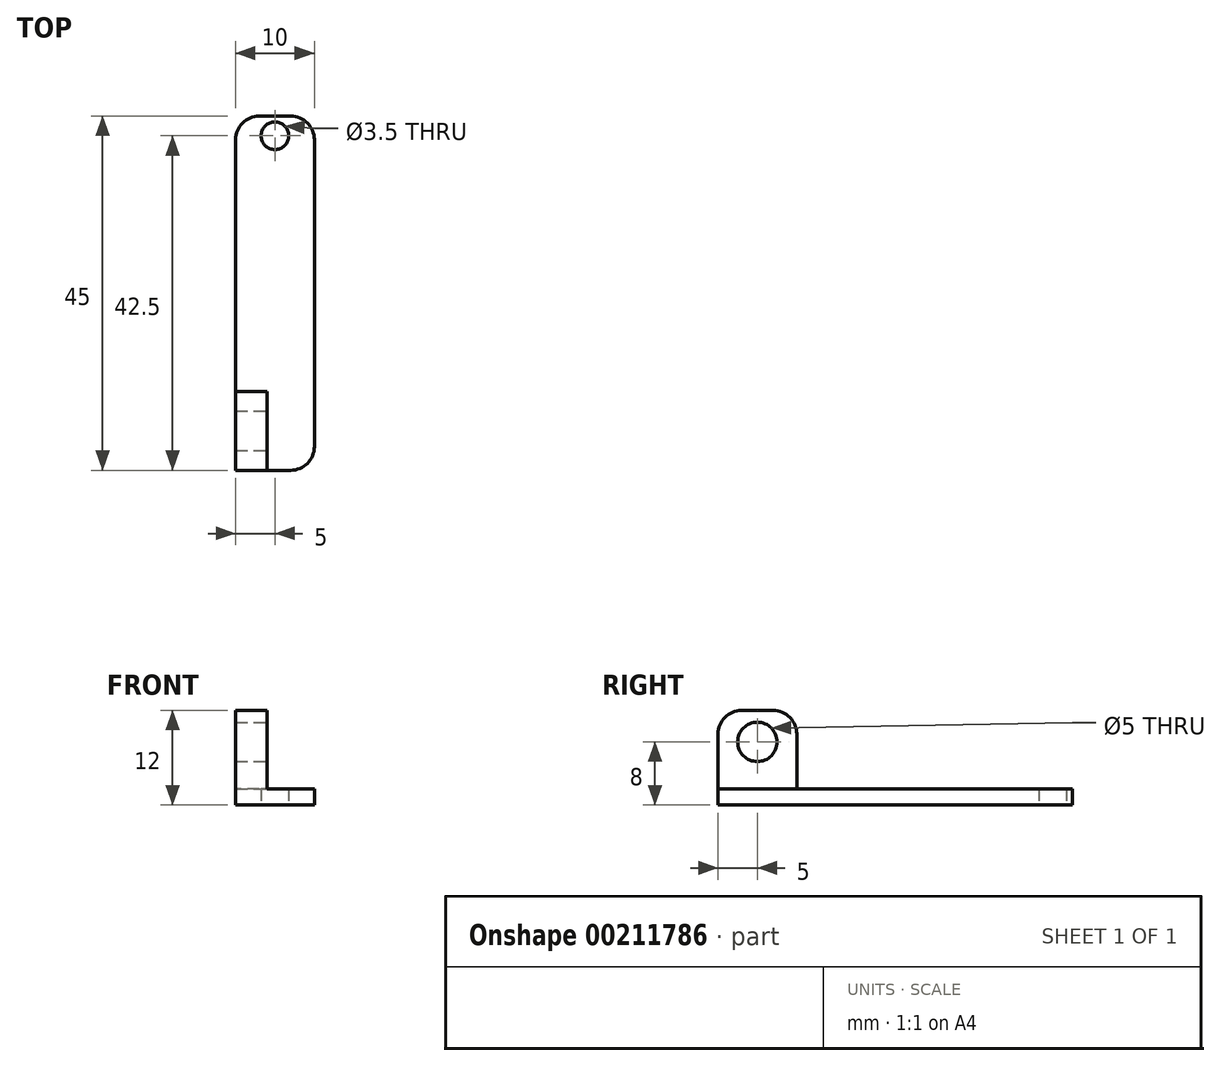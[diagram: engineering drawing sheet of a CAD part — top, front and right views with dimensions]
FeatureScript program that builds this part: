
annotation { "Feature Type Name" : "Feature", "Feature Type Description" : "" }
export const myFeature = defineFeature(function(context is Context, id is Id, definition is map)
    precondition{}
    {
        {
            var Q0;
            Q0=qCreatedBy(makeId("Top.planeOp"),FACE);
            var sketch = newSketch(context, id + "F0", { "sketchPlane" : qUnion([Q0])});
            skLineSegment(sketch, "E0.bottom", {"start": v(0, 0) * mm, "end": v(10, 0) * mm});
            skLineSegment(sketch, "E0.top", {"start": v(0, 45) * mm, "end": v(10, 45) * mm});
            skLineSegment(sketch, "E0.left", {"start": v(0, 0) * mm, "end": v(0, 45) * mm});
            skLineSegment(sketch, "E0.right", {"start": v(10, 0) * mm, "end": v(10, 45) * mm});
            skCircle(sketch, "E1", {"center": v(5, 42.5) * mm, "radius": 1.75 * mm});
            skSolve(sketch);
        }
        {
            var Q0;
            Q0=makeQuery(id+"F0.imprint","IMPRINT",FACE,{"disambiguationData":[TD([[makeQuery(id+"F0.imprint","IMPRINT",EDGE,{"derivedFrom":sQuery(id+"F0.wireOp",EDGE,"E0.bottom")}),1.0]])]});
            extrude(context, id + "F1", {"entities" : qUnion([Q0]), "depth" : 2 * mm});
        }
        {
            var Q0;
            Q0=makeQuery(id+"F1.opExtrude","CAP_FACE",FACE,{"disambiguationData":[OSD([sQuery(id+"F0.wireOp",EDGE,"E0.bottom"),sQuery(id+"F0.wireOp",EDGE,"E0.top"),sQuery(id+"F0.wireOp",EDGE,"E0.left"),sQuery(id+"F0.wireOp",EDGE,"E0.right"),sQuery(id+"F0.wireOp",EDGE,"E1")])],"isStart":false});
            var sketch = newSketch(context, id + "F2", { "sketchPlane" : qUnion([Q0])});
            skLineSegment(sketch, "E2.bottom", {"start": v(0, 0) * mm, "end": v(4, 0) * mm});
            skLineSegment(sketch, "E2.top", {"start": v(0, 10) * mm, "end": v(4, 10) * mm});
            skLineSegment(sketch, "E2.left", {"start": v(0, 0) * mm, "end": v(0, 10) * mm});
            skLineSegment(sketch, "E2.right", {"start": v(4, 0) * mm, "end": v(4, 10) * mm});
            skSolve(sketch);
        }
        {
            var Q0;
            Q0=makeQuery(id+"F2.imprint","IMPRINT",FACE,{"disambiguationData":[TD([[makeQuery(id+"F2.imprint","IMPRINT",EDGE,{"derivedFrom":sQuery(id+"F2.wireOp",EDGE,"E2.bottom")}),1.0]])]});
            extrude(context, id + "F3", {"entities" : qUnion([Q0]), "operationType" : NewBodyOperationType.ADD, "depth" : 10 * mm});
        }
        {
            var Q0;
            Q0=makeQuery(id+"F1.opExtrude","SWEPT_EDGE",EDGE,{"disambiguationData":[OSD([sQuery(id+"F0.wireOp",EDGE,"E0.top"),sQuery(id+"F0.wireOp",EDGE,"E0.right")])]});
            var Q1;
            Q1=makeQuery(id+"F1.opExtrude","SWEPT_EDGE",EDGE,{"disambiguationData":[OSD([sQuery(id+"F0.wireOp",EDGE,"E0.bottom"),sQuery(id+"F0.wireOp",EDGE,"E0.right")])]});
            var Q2;
            Q2=makeQuery(id+"F1.opExtrude","SWEPT_EDGE",EDGE,{"disambiguationData":[OSD([sQuery(id+"F0.wireOp",EDGE,"E0.top"),sQuery(id+"F0.wireOp",EDGE,"E0.left")])]});
            var Q3;
            Q3=makeQuery(id+"F3.opExtrude","CAP_EDGE",EDGE,{"disambiguationData":[OSD([sQuery(id+"F2.wireOp",EDGE,"E2.bottom")])],"isStart":false});
            var Q4;
            Q4=makeQuery(id+"F3.opExtrude","CAP_EDGE",EDGE,{"disambiguationData":[OSD([sQuery(id+"F2.wireOp",EDGE,"E2.top")])],"isStart":false});
            fillet(context, id + "F4", {"entities" : qUnion([Q0, Q1, Q2, Q3, Q4]), "radius" : 3 * mm, "tangentPropagation" : true, "allowEdgeOverflow" : false});
        }
        {
            var Q0;
            Q0=makeQuery(id+"F3.opExtrude","SWEPT_FACE",FACE,{"disambiguationData":[OSD([sQuery(id+"F2.wireOp",EDGE,"E2.right")])]});
            var sketch = newSketch(context, id + "F5", { "sketchPlane" : qUnion([Q0])});
            skCircle(sketch, "E3", {"center": v(5, 8) * mm, "radius": 2.5 * mm});
            skSolve(sketch);
        }
        {
            var Q0;
            Q0=makeQuery(id+"F5.imprint","IMPRINT",FACE,{"disambiguationData":[TD([[makeQuery(id+"F5.imprint","IMPRINT",EDGE,{"derivedFrom":sQuery(id+"F5.wireOp",EDGE,"E3")}),1.0]])]});
            extrude(context, id + "F6", {"entities" : qUnion([Q0]), "operationType" : NewBodyOperationType.REMOVE, "oppositeDirection" : true, "depth" : 25.4 * mm});
        }
    });
